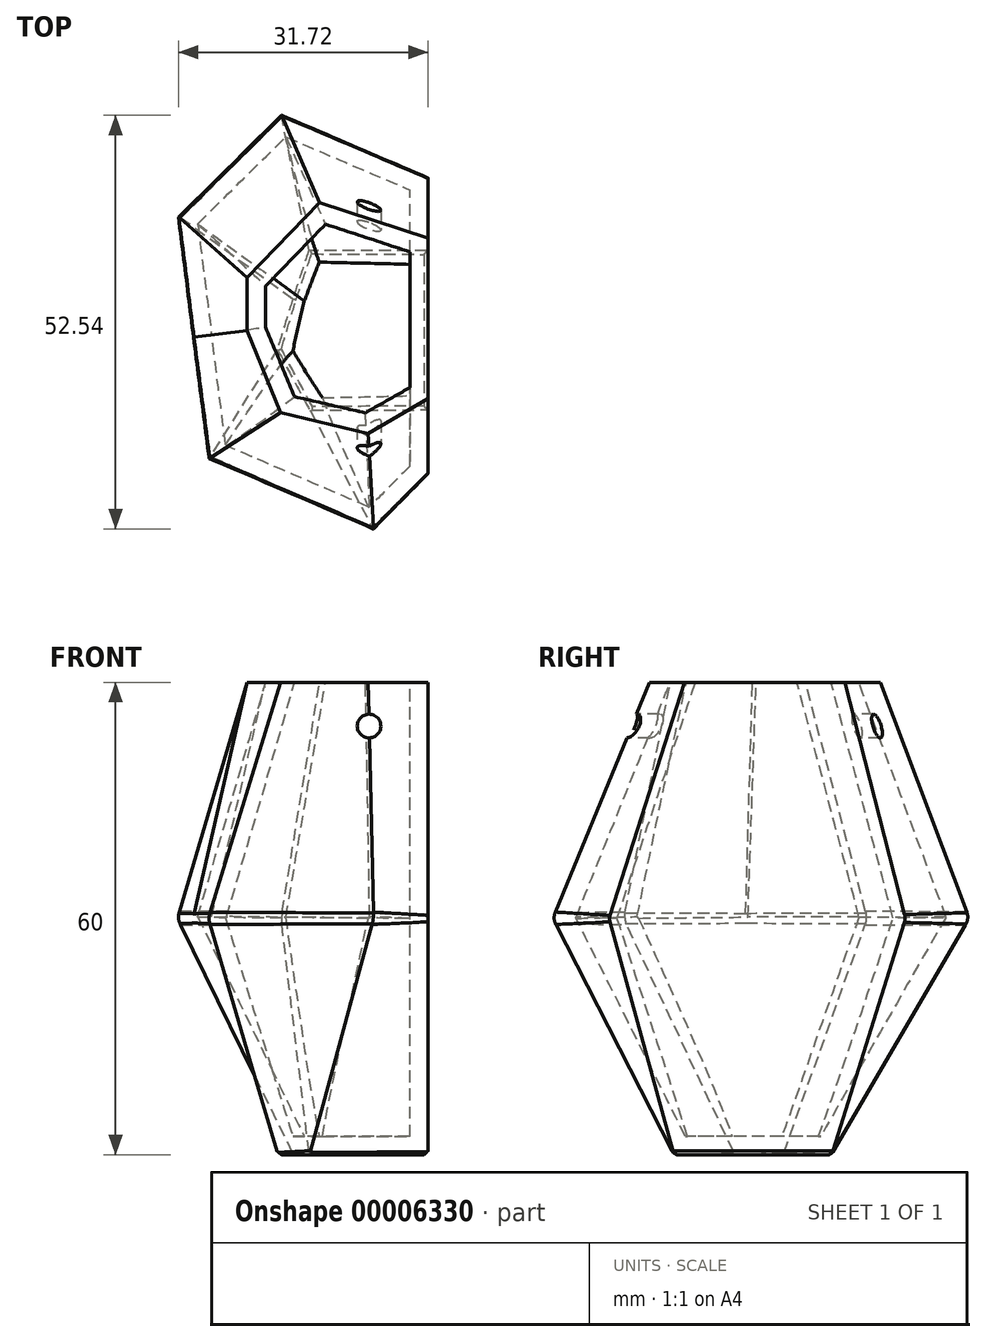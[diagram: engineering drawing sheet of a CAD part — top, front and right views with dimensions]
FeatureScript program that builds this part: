
annotation { "Feature Type Name" : "Feature", "Feature Type Description" : "" }
export const myFeature = defineFeature(function(context is Context, id is Id, definition is map)
    precondition{}
    {
        {
            var Q0;
            Q0=qCreatedBy(makeId("Top.planeOp"),FACE);
            var sketch = newSketch(context, id + "F0", { "sketchPlane" : qUnion([Q0])});
            skLineSegment(sketch, "E0", {"start": v(0, 19.45) * mm, "end": v(0, -18.2) * mm});
            skLineSegment(sketch, "E1", {"start": v(0, -18.2) * mm, "end": v(-6.9, -25.36) * mm});
            skLineSegment(sketch, "E2", {"start": v(-6.9, -25.36) * mm, "end": v(-27.93, -16.35) * mm});
            skLineSegment(sketch, "E3", {"start": v(-27.93, -16.35) * mm, "end": v(-31.85, 14.6) * mm});
            skLineSegment(sketch, "E4", {"start": v(-31.85, 14.6) * mm, "end": v(-18.69, 27.53) * mm});
            skLineSegment(sketch, "E5", {"start": v(-18.69, 27.53) * mm, "end": v(0, 19.45) * mm});
            skLineSegment(sketch, "E6", {"start": v(0, 0) * mm, "end": v(-30, 0) * mm, "construction": true});
            skSolve(sketch);
        }
        {
            var Q0;
            Q0=qCreatedBy(makeId("Top.planeOp"),FACE);
            cPlane(context, id + "F1", {"entities" : qUnion([Q0]), "cplaneType" : CPlaneType.OFFSET, "offset" : 30 * mm, "width" : 150 * mm, "height" : 150 * mm});
        }
        {
            var Q0;
            Q0=qCreatedBy(id+"F1.planeOp",FACE);
            var sketch = newSketch(context, id + "F2", { "sketchPlane" : qUnion([Q0])});
            skLineSegment(sketch, "E7", {"start": v(0, 11.73) * mm, "end": v(0, -8.66) * mm});
            skLineSegment(sketch, "E8", {"start": v(0, -8.66) * mm, "end": v(-7.62, -13.07) * mm});
            skLineSegment(sketch, "E9", {"start": v(-7.62, -13.07) * mm, "end": v(-18.78, -10.42) * mm});
            skLineSegment(sketch, "E10", {"start": v(-18.78, -10.42) * mm, "end": v(-23.03, 0) * mm});
            skLineSegment(sketch, "E11", {"start": v(-23.03, 0) * mm, "end": v(-23.03, 6.74) * mm});
            skLineSegment(sketch, "E12", {"start": v(-23.03, 6.74) * mm, "end": v(-13.79, 16.28) * mm});
            skLineSegment(sketch, "E13", {"start": v(-13.79, 16.28) * mm, "end": v(0, 11.73) * mm});
            skSolve(sketch);
        }
        {
            var Q0;
            Q0=qCreatedBy(makeId("Top.planeOp"),FACE);
            cPlane(context, id + "F3", {"entities" : qUnion([Q0]), "cplaneType" : CPlaneType.OFFSET, "offset" : 30 * mm, "oppositeDirection" : true, "width" : 150 * mm, "height" : 150 * mm});
        }
        {
            var Q0;
            Q0=qCreatedBy(id+"F3.planeOp",FACE);
            var sketch = newSketch(context, id + "F4", { "sketchPlane" : qUnion([Q0])});
            skLineSegment(sketch, "E14", {"start": v(0, 10.04) * mm, "end": v(0, -9.96) * mm});
            skLineSegment(sketch, "E15", {"start": v(0, -9.96) * mm, "end": v(-15.1, -9.96) * mm});
            skLineSegment(sketch, "E16", {"start": v(-15.1, 10.04) * mm, "end": v(0, 10.04) * mm});
            skLineSegment(sketch, "E17", {"start": v(-15.1, -9.96) * mm, "end": v(-19.06, -2.23) * mm});
            skLineSegment(sketch, "E18", {"start": v(-19.06, -2.23) * mm, "end": v(-15.1, 10.04) * mm});
            skLineSegment(sketch, "E19", {"start": v(-10.12, 10.04) * mm, "end": v(-10.12, -9.96) * mm, "construction": true});
            skSolve(sketch);
        }
        {
            var Q0;
            Q0=makeQuery(id+"F4.imprint","IMPRINT",FACE,{"disambiguationData":[TD([[makeQuery(id+"F4.imprint","IMPRINT",EDGE,{"derivedFrom":sQuery(id+"F4.wireOp",EDGE,"E14")}),-1.0]])]});
            var Q1;
            Q1=makeQuery(id+"F0.imprint","IMPRINT",FACE,{"disambiguationData":[TD([[makeQuery(id+"F0.imprint","IMPRINT",EDGE,{"derivedFrom":sQuery(id+"F0.wireOp",EDGE,"E0")}),-1.0]])]});
            loft(context, id + "F5", {"sheetProfilesArray" : [{ "sheetProfileEntities" : qUnion([Q0]) }, { "sheetProfileEntities" : qUnion([Q1]) }]});
        }
        {
            var Q0;
            Q0=makeQuery(id+"F0.imprint","IMPRINT",FACE,{"disambiguationData":[TD([[makeQuery(id+"F0.imprint","IMPRINT",EDGE,{"derivedFrom":sQuery(id+"F0.wireOp",EDGE,"E0")}),-1.0]])]});
            var Q1;
            Q1=makeQuery(id+"F2.imprint","IMPRINT",FACE,{"disambiguationData":[TD([[makeQuery(id+"F2.imprint","IMPRINT",EDGE,{"derivedFrom":sQuery(id+"F2.wireOp",EDGE,"E7")}),-1.0]])]});
            loft(context, id + "F6", {"operationType" : NewBodyOperationType.ADD, "sheetProfilesArray" : [{ "sheetProfileEntities" : qUnion([Q0]) }, { "sheetProfileEntities" : qUnion([Q1]) }]});
        }
        {
            var Q0;
            {var subQ0=sQuery(id+"F0.wireOp",EDGE,"E1");var subQ1=sQuery(id+"F0.wireOp",EDGE,"E2");var subQ2=sQuery(id+"F0.wireOp",EDGE,"E3");Q0=makeQuery(id+"F6.boolean.opBoolean","MERGE",EDGE,{"derivedFrom":[makeQuery(id+"F5.opLoft","MID_CAP_EDGE",EDGE,{"disambiguationData":[OSD([subQ0,subQ1,subQ2])],"capPos":1.0}),makeQuery(id+"F6.opLoft","MID_CAP_EDGE",EDGE,{"disambiguationData":[OSD([subQ0,subQ1,subQ2])],"capPos":0.0})]});}
            var Q1;
            {var subQ0=sQuery(id+"F0.wireOp",EDGE,"E0");var subQ1=sQuery(id+"F0.wireOp",EDGE,"E1");var subQ2=sQuery(id+"F0.wireOp",EDGE,"E2");Q1=makeQuery(id+"F6.boolean.opBoolean","MERGE",EDGE,{"derivedFrom":[makeQuery(id+"F5.opLoft","MID_CAP_EDGE",EDGE,{"disambiguationData":[OSD([subQ0,subQ1,subQ2])],"capPos":1.0}),makeQuery(id+"F6.opLoft","MID_CAP_EDGE",EDGE,{"disambiguationData":[OSD([subQ0,subQ1,subQ2])],"capPos":0.0})]});}
            var Q2;
            {var subQ0=sQuery(id+"F0.wireOp",EDGE,"E2");var subQ1=sQuery(id+"F0.wireOp",EDGE,"E3");var subQ2=sQuery(id+"F0.wireOp",EDGE,"E4");Q2=makeQuery(id+"F6.boolean.opBoolean","MERGE",EDGE,{"derivedFrom":[makeQuery(id+"F5.opLoft","MID_CAP_EDGE",EDGE,{"disambiguationData":[OSD([subQ0,subQ1,subQ2])],"capPos":1.0}),makeQuery(id+"F6.opLoft","MID_CAP_EDGE",EDGE,{"disambiguationData":[OSD([subQ0,subQ1,subQ2])],"capPos":0.0})]});}
            var Q3;
            {var subQ0=sQuery(id+"F0.wireOp",EDGE,"E3");var subQ1=sQuery(id+"F0.wireOp",EDGE,"E4");var subQ2=sQuery(id+"F0.wireOp",EDGE,"E5");Q3=makeQuery(id+"F6.boolean.opBoolean","MERGE",EDGE,{"derivedFrom":[makeQuery(id+"F5.opLoft","MID_CAP_EDGE",EDGE,{"disambiguationData":[OSD([subQ0,subQ1,subQ2])],"capPos":1.0}),makeQuery(id+"F6.opLoft","MID_CAP_EDGE",EDGE,{"disambiguationData":[OSD([subQ0,subQ1,subQ2])],"capPos":0.0})]});}
            var Q4;
            {var subQ0=sQuery(id+"F0.wireOp",EDGE,"E4");var subQ1=sQuery(id+"F0.wireOp",EDGE,"E5");Q4=makeQuery(id+"F6.boolean.opBoolean","MERGE",EDGE,{"derivedFrom":[makeQuery(id+"F5.opLoft","MID_CAP_EDGE",EDGE,{"disambiguationData":[OSD([sQuery(id+"F0.wireOp",EDGE,"E0"),subQ0,subQ1])],"capPos":1.0}),makeQuery(id+"F6.opLoft","MID_CAP_EDGE",EDGE,{"disambiguationData":[OSD([subQ0,subQ1,sQuery(id+"F2.wireOp",EDGE,"E12"),sQuery(id+"F2.wireOp",EDGE,"E13")])],"capPos":0.0})]});}
            var Q5;
            {var subQ0=sQuery(id+"F0.wireOp",EDGE,"E0");var subQ1=sQuery(id+"F0.wireOp",EDGE,"E5");Q5=makeQuery(id+"F6.boolean.opBoolean","MERGE",EDGE,{"derivedFrom":[makeQuery(id+"F5.opLoft","MID_CAP_EDGE",EDGE,{"disambiguationData":[OSD([subQ0,sQuery(id+"F0.wireOp",EDGE,"E4"),subQ1])],"capPos":1.0}),makeQuery(id+"F6.opLoft","MID_CAP_EDGE",EDGE,{"disambiguationData":[OSD([subQ0,subQ1,sQuery(id+"F2.wireOp",EDGE,"E12"),sQuery(id+"F2.wireOp",EDGE,"E13")])],"capPos":0.0})]});}
            fillet(context, id + "F7", {"entities" : qUnion([Q0, Q1, Q2, Q3, Q4, Q5]), "radius" : 2 * mm, "tangentPropagation" : true, "allowEdgeOverflow" : false});
        }
        {
            var Q0;
            Q0=makeQuery(id+"F6.opLoft","CAP_FACE",FACE,{"disambiguationData":[OSD([makeQuery(id+"F2.imprint","IMPRINT",FACE,{"disambiguationData":[TD([[makeQuery(id+"F2.imprint","IMPRINT",EDGE,{"derivedFrom":sQuery(id+"F2.wireOp",EDGE,"E7")}),-1.0]])]})])],"isStart":true});
            shell(context, id + "F8", {"entities" : qUnion([Q0]), "thickness" : 2.3 * mm});
        }
        {
            var Q0;
            Q0=qCreatedBy(makeId("Front.planeOp"),FACE);
            var sketch = newSketch(context, id + "F9", { "sketchPlane" : qUnion([Q0])});
            skCircle(sketch, "E20", {"center": v(-7.51, 24.45) * mm, "radius": 1.5 * mm});
            skSolve(sketch);
        }
        {
            var Q0;
            Q0=makeQuery(id+"F9.imprint","IMPRINT",FACE,{"disambiguationData":[TD([[makeQuery(id+"F9.imprint","IMPRINT",EDGE,{"derivedFrom":sQuery(id+"F9.wireOp",EDGE,"E20")}),1.0]])]});
            extrude(context, id + "F10", {"entities" : qUnion([Q0]), "operationType" : NewBodyOperationType.REMOVE, "endBound" : BoundingType.SYMMETRIC, "oppositeDirection" : true, "depth" : 100 * mm});
        }
        {
            var Q0;
            Q0=makeQuery(id+"F5.opLoft","CAP_FACE",FACE,{"disambiguationData":[OSD([makeQuery(id+"F4.imprint","IMPRINT",FACE,{"disambiguationData":[TD([[makeQuery(id+"F4.imprint","IMPRINT",EDGE,{"derivedFrom":sQuery(id+"F4.wireOp",EDGE,"E14")}),-1.0]])]})])],"isStart":true});
            chamfer(context, id + "F11", {"entities" : qUnion([Q0]), "width" : 0.5 * mm, "tangentPropagation" : true});
        }
    });
